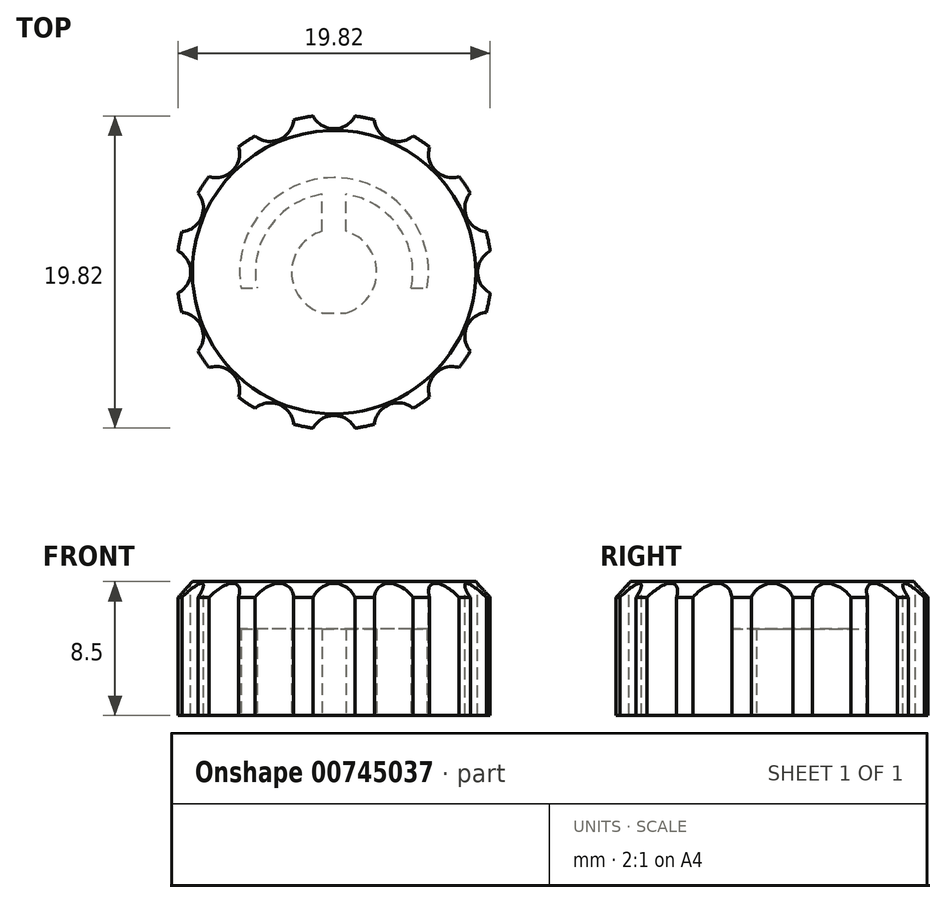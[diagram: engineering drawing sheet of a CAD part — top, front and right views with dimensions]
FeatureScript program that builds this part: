
annotation { "Feature Type Name" : "Feature", "Feature Type Description" : "" }
export const myFeature = defineFeature(function(context is Context, id is Id, definition is map)
    precondition{}
    {
        {
            var Q0;
            Q0=qCreatedBy(makeId("Top.planeOp"),FACE);
            var sketch = newSketch(context, id + "F0", { "sketchPlane" : qUnion([Q0])});
            skArc(sketch, "E0", {"start": v(-0.75, 2.6) * mm, "mid": v(-2.7, 0) * mm, "end": v(-0.75, -2.6) * mm});
            skArc(sketch, "E1", {"start": v(-0.75, 4.94) * mm, "mid": v(-4.1, 2.86) * mm, "end": v(-4.9, -1) * mm});
            skLineSegment(sketch, "E2.left", {"start": v(0.75, 2.6) * mm, "end": v(0.75, 4.94) * mm});
            skLineSegment(sketch, "E2.right", {"start": v(-0.75, 2.6) * mm, "end": v(-0.75, 4.94) * mm});
            skArc(sketch, "E3", {"start": v(5.92, -1) * mm, "mid": v(0, 6) * mm, "end": v(-5.92, -1) * mm});
            skCircle(sketch, "E4", {"center": v(0, 0) * mm, "radius": 10 * mm});
            skArc(sketch, "E5.trimOffspring", {"start": v(4.9, -1) * mm, "mid": v(4.1, 2.86) * mm, "end": v(0.75, 4.94) * mm});
            skArc(sketch, "E6.trimOffspring", {"start": v(0.75, -2.6) * mm, "mid": v(2.7, 0) * mm, "end": v(0.75, 2.6) * mm});
            skLineSegment(sketch, "E7", {"start": v(-5.92, -1) * mm, "end": v(-4.9, -1) * mm});
            skLineSegment(sketch, "E8", {"start": v(4.9, -1) * mm, "end": v(5.92, -1) * mm});
            skLineSegment(sketch, "E9", {"start": v(-0.75, -2.6) * mm, "end": v(0.75, -2.6) * mm});
            skSolve(sketch);
        }
        {
            var Q0;
            Q0=makeQuery(id+"F0.imprint","IMPRINT",FACE,{"disambiguationData":[TD([[makeQuery(id+"F0.imprint","IMPRINT",EDGE,{"derivedFrom":sQuery(id+"F0.wireOp",EDGE,"E0")}),-1.0]])]});
            var Q1;
            Q1=makeQuery(id+"F0.imprint","IMPRINT",FACE,{"disambiguationData":[TD([[makeQuery(id+"F0.imprint","IMPRINT",EDGE,{"derivedFrom":sQuery(id+"F0.wireOp",EDGE,"E2.left")}),-1.0]])]});
            var Q2;
            Q2=makeQuery(id+"F0.imprint","IMPRINT",FACE,{"disambiguationData":[TD([[makeQuery(id+"F0.imprint","IMPRINT",EDGE,{"derivedFrom":sQuery(id+"F0.wireOp",EDGE,"E3")}),-1.0]])]});
            extrude(context, id + "F1", {"entities" : qUnion([Q0, Q1, Q2]), "depth" : 5.5 * mm, "offsetDistance" : 25 * mm});
        }
        {
            var Q0;
            Q0=makeQuery(id+"F1.opExtrude","CAP_FACE",FACE,{"disambiguationData":[OSD([sQuery(id+"F0.wireOp",EDGE,"E3"),sQuery(id+"F0.wireOp",EDGE,"E4"),sQuery(id+"F0.wireOp",EDGE,"v1sKEDbx-lZMi-Krtm-SMOo-CMrNC3qRjQl3")])],"isStart":false});
            var sketch = newSketch(context, id + "F2", { "sketchPlane" : qUnion([Q0])});
            skCircle(sketch, "E10", {"center": v(0, 0) * mm, "radius": 9 * mm});
            skSolve(sketch);
        }
        {
            var Q0;
            Q0 = qSketchRegion(id + "F2", true);
            var Q1;
            Q1=makeQuery(id+"F2.imprint","IMPRINT",FACE,{"disambiguationData":[TD([[makeQuery(id+"F2.imprint","IMPRINT",EDGE,{"derivedFrom":sQuery(id+"F2.wireOp",EDGE,"E10")}),-1.0]])]});
            extrude(context, id + "F3", {"entities" : qUnion([Q0, Q1]), "operationType" : NewBodyOperationType.ADD, "depth" : 3 * mm, "offsetDistance" : 25 * mm});
        }
        {
            var Q0;
            Q0=makeQuery(id+"F3.opExtrude","CAP_EDGE",EDGE,{"disambiguationData":[OSD([sQuery(id+"F0.wireOp",EDGE,"E4")])],"isStart":false});
            chamfer(context, id + "F4", {"entities" : qUnion([Q0]), "width" : 1 * mm, "tangentPropagation" : true});
        }
        {
            var Q0;
            Q0=makeQuery(id+"F3.opExtrude","CAP_FACE",FACE,{"disambiguationData":[OSD([sQuery(id+"F0.wireOp",EDGE,"E4")])],"isStart":false});
            var sketch = newSketch(context, id + "F5", { "sketchPlane" : qUnion([Q0])});
            skCircle(sketch, "E11", {"center": v(-7.5, 7.5) * mm, "radius": 1.5 * mm});
            skSolve(sketch);
        }
        {
            var Q0;
            Q0=makeQuery(id+"F5.imprint","IMPRINT",FACE,{"disambiguationData":[TD([[makeQuery(id+"F5.imprint","IMPRINT",EDGE,{"derivedFrom":sQuery(id+"F5.wireOp",EDGE,"E11")}),1.0]])]});
            extrude(context, id + "F6", {"entities" : qUnion([Q0]), "oppositeDirection" : true, "depth" : 10 * mm, "offsetDistance" : 25 * mm});
        }
        {
            var Q0;
            Q0=makeQuery(id+"F6.opExtrude","SWEPT_BODY",BODY,{"disambiguationData":[OSD([sQuery(id+"F5.wireOp",EDGE,"E11")])]});
            var Q1;
            {var subQ0=sQuery(id+"F0.wireOp",EDGE,"E4");Q1=makeQuery(id+"F4.opChamfer","BLEND_EDGE",EDGE,{"blendedFrom":[makeQuery(id+"F3.opExtrude","CAP_EDGE",EDGE,{"disambiguationData":[OSD([subQ0])],"isStart":false}),makeQuery(id+"F3.opExtrude","CAP_FACE",FACE,{"disambiguationData":[OSD([subQ0])],"isStart":false})],"blendedInto":[makeQuery(id+"F3.opExtrude","CAP_FACE",FACE,{"disambiguationData":[OSD([subQ0])],"isStart":false})]});}
            circularPattern(context, id + "F7", {"operationType" : NewBodyOperationType.REMOVE, "entities" : qUnion([Q0]), "axis" : qUnion([Q1]), "angle" : 360 * degree, "instanceCount" : 16, "equalSpace" : true});
        }
    });
